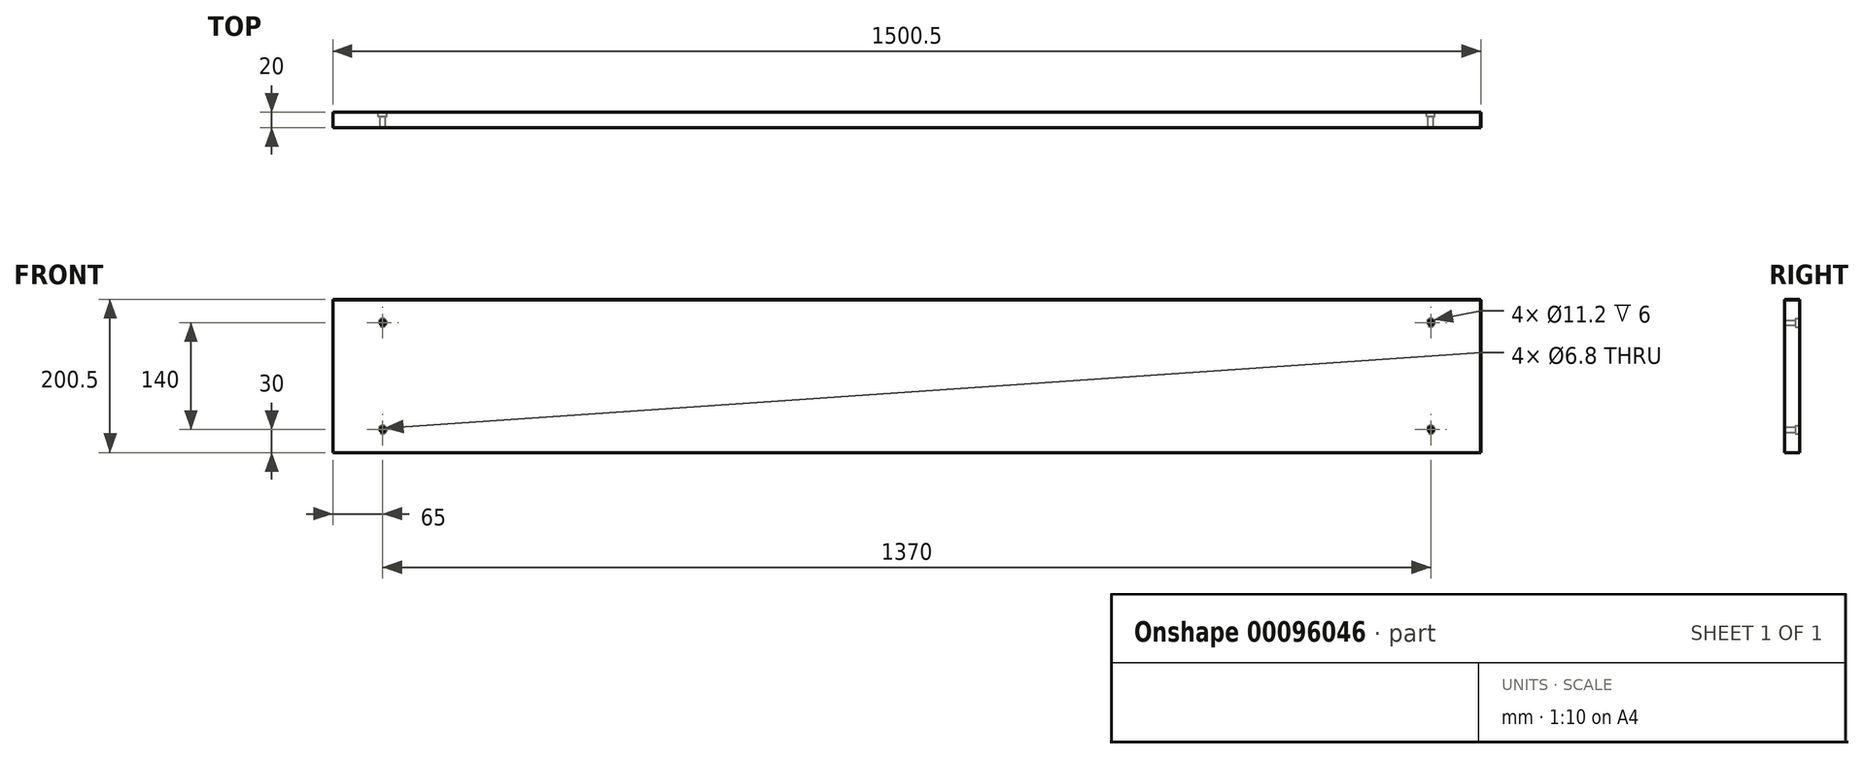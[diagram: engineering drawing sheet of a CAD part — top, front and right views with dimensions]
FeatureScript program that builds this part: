
annotation { "Feature Type Name" : "Feature", "Feature Type Description" : "" }
export const myFeature = defineFeature(function(context is Context, id is Id, definition is map)
    precondition{}
    {
        {
            var Q0;
            Q0=qCreatedBy(makeId("Front.planeOp"),FACE);
            var sketch = newSketch(context, id + "F0", { "sketchPlane" : qUnion([Q0])});
            skLineSegment(sketch, "E0.bottom", {"start": v(750, -100) * mm, "end": v(-750, -100) * mm});
            skLineSegment(sketch, "E0.top", {"start": v(750, 100) * mm, "end": v(-750, 100) * mm});
            skLineSegment(sketch, "E0.left", {"start": v(750, -100) * mm, "end": v(750, 100) * mm});
            skLineSegment(sketch, "E0.right", {"start": v(-750, -100) * mm, "end": v(-750, 100) * mm});
            skPoint(sketch, "E0.middle", {"position": v(0, 0) * mm});
            skSolve(sketch);
        }
        {
            var Q0;
            Q0 = qSketchRegion(id + "F0", true);
            extrude(context, id + "F1", {"entities" : qUnion([Q0]), "depth" : 20 * mm});
        }
        {
            var Q0;
            Q0=makeQuery(id+"F1.opExtrude","CAP_FACE",FACE,{"disambiguationData":[OSD([sQuery(id+"F0.wireOp",EDGE,"E0.bottom"),sQuery(id+"F0.wireOp",EDGE,"E0.top"),sQuery(id+"F0.wireOp",EDGE,"E0.left"),sQuery(id+"F0.wireOp",EDGE,"E0.right")])],"isStart":true});
            var sketch = newSketch(context, id + "F2", { "sketchPlane" : qUnion([Q0])});
            skCircle(sketch, "E1", {"center": v(-685, 70) * mm, "radius": 5.6 * mm});
            skCircle(sketch, "E2.MirrorC", {"center": v(-685, -70) * mm, "radius": 5.6 * mm});
            skCircle(sketch, "E3.MirrorC", {"center": v(685, 70) * mm, "radius": 5.6 * mm});
            skCircle(sketch, "E4.MirrorC", {"center": v(685, -70) * mm, "radius": 5.6 * mm});
            skSolve(sketch);
        }
        {
            var Q0;
            Q0=makeQuery(id+"F2.imprint","IMPRINT",FACE,{"disambiguationData":[TD([[makeQuery(id+"F2.imprint","IMPRINT",EDGE,{"derivedFrom":sQuery(id+"F2.wireOp",EDGE,"E1")}),-1.0]])]});
            var sketch = newSketch(context, id + "F3", { "sketchPlane" : qUnion([Q0])});
            skCircle(sketch, "E5", {"center": v(-685, 70) * mm, "radius": 3.4 * mm});
            skCircle(sketch, "E6.MirrorC", {"center": v(-685, -70) * mm, "radius": 3.4 * mm});
            skCircle(sketch, "E7.MirrorC", {"center": v(685, 70) * mm, "radius": 3.4 * mm});
            skCircle(sketch, "E8.MirrorC", {"center": v(685, -70) * mm, "radius": 3.4 * mm});
            skSolve(sketch);
        }
        {
            var Q0;
            Q0 = qSketchRegion(id + "F2", true);
            extrude(context, id + "F4", {"entities" : qUnion([Q0]), "operationType" : NewBodyOperationType.REMOVE, "oppositeDirection" : true, "depth" : 6 * mm});
        }
        {
            var Q0;
            Q0 = qSketchRegion(id + "F3", true);
            extrude(context, id + "F5", {"entities" : qUnion([Q0]), "operationType" : NewBodyOperationType.REMOVE, "endBound" : BoundingType.THROUGH_ALL, "oppositeDirection" : true, "depth" : 25 * mm});
        }
        {
            var Q0;
            Q0=makeQuery(id+"F1.opExtrude","SWEPT_FACE",FACE,{"disambiguationData":[OSD([sQuery(id+"F0.wireOp",EDGE,"E0.top")])]});
            var sketch = newSketch(context, id + "F6", { "sketchPlane" : qUnion([Q0])});
            skLineSegment(sketch, "E9.bottom", {"start": v(-750, 0) * mm, "end": v(750, 0) * mm});
            skLineSegment(sketch, "E9.top", {"start": v(-750, -20) * mm, "end": v(750, -20) * mm});
            skLineSegment(sketch, "E9.left", {"start": v(-750, 0) * mm, "end": v(-750, -20) * mm});
            skLineSegment(sketch, "E9.right", {"start": v(750, 0) * mm, "end": v(750, -20) * mm});
            skSolve(sketch);
        }
        {
            var Q0;
            Q0 = qSketchRegion(id + "F6", true);
            extrude(context, id + "F7", {"entities" : qUnion([Q0]), "depth" : .5 * mm});
        }
        {
            var Q0;
            Q0=makeQuery(id+"F1.opExtrude","SWEPT_FACE",FACE,{"disambiguationData":[OSD([sQuery(id+"F0.wireOp",EDGE,"E0.left")])]});
            var sketch = newSketch(context, id + "F8", { "sketchPlane" : qUnion([Q0])});
            skLineSegment(sketch, "E10.bottom", {"start": v(0, 100) * mm, "end": v(-20, 100) * mm});
            skLineSegment(sketch, "E10.top", {"start": v(0, -100) * mm, "end": v(-20, -100) * mm});
            skLineSegment(sketch, "E10.left", {"start": v(0, 100) * mm, "end": v(0, -100) * mm});
            skLineSegment(sketch, "E10.right", {"start": v(-20, 100) * mm, "end": v(-20, -100) * mm});
            skSolve(sketch);
        }
        {
            var Q0;
            Q0 = qSketchRegion(id + "F8", true);
            extrude(context, id + "F9", {"entities" : qUnion([Q0]), "depth" : 0.5 * mm});
        }
    });
